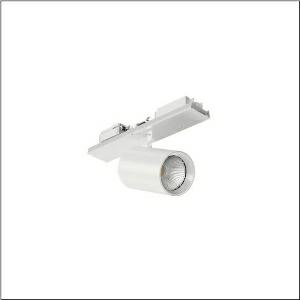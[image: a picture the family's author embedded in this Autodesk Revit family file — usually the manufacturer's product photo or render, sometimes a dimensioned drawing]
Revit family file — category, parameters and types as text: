
# Revit family: licross_r__spot_31_51sl127a43b_2c6e
name_source: partatom
category: Lighting Fixtures
units: mm (PartAtom-declared; Revit-internal decimal feet)

## family parameters
Cut with Voids When Loaded = No
Host = Face
Light Source = No
Part Type = Normal
Room Calculation Point = No
Round Connector Dimension = Use Diameter
Shared = No

## types (1)
- --- (1 x LED, 3650 lm, 28 W, 4000K)
    Apparent Load = 28 VA
    CIE Flux Codes = 93 97 99 100 100
    Color Rendering = 90
    Color Temperature = 4000K
    Default Elevation = 1800 mm
    Description = Licross® Spot 31, directional spotlight, light control with lens, of plastic, LED rated luminous flux: 3.650lm, light colour: 940, with plug, 3-pole, with phase selection, mains connection: 220..240V, AC, 50/60Hz, of aluminium, traffic white (RAL 9016), length: 300mm, diameter: 90mm, protection rating (complete): IP20, insulation class (complete): insulation class I (protective earthing), certification: CE, packaging unit: 1 piece
    Height = 175 mm
    Lamp = 1 x LED
    Lamp Light Flux = 3650 lm
    Lamp Power = 28 W
    Lamp count = 1
    Length = 90 mm
    Luminous efficacy = 130 lm/W
    Manufacturer = Siteco
    ModVariant = No
    Model = 51SL127A43B
    Mounting Place = Ceiling
    Mounting Type = Pendant
    Number of Poles = 1
    OnlyDefault = Yes
    Power Factor = 1
    Product Name = Licross® Spot 31
    Product group = directional spotlight
    ProductGroupID = 906
    Protection Class = Protection class I
    Protection Degree = IP 20
    RLX_Detail_Level = 1
    RLX_Emergency_Light_Flux = 0 lm
    RLX_Emergency_Type = 0
    RLX_Emergency_Type_DB = No
    RlxData = <blob elided: 14901 chars, md5=9e8d82e2>
    Socket = socket
    Standby Power = 0 W
    System Light Flux = 3650 lm
    System Power = 28 W
    Type Comments = factory setting: luminous flux: 100 % | (ON | ON | ON) | 700 mA
    Type Image = l_1245720.jpg
    URL = http://relux.com
    VarID = @adj_132808
    Voltage = 0 V
    Weight = 0.00 kg
    Width = 0 mm  [stored 0 ft]

note: [stored X ft] marks values corroborated as IEEE doubles in the binary element streams (Revit-internal decimal feet)

## geometry (parser evidence)
native form markers: Sweep x11
no freeform markers — native parametric forms only
